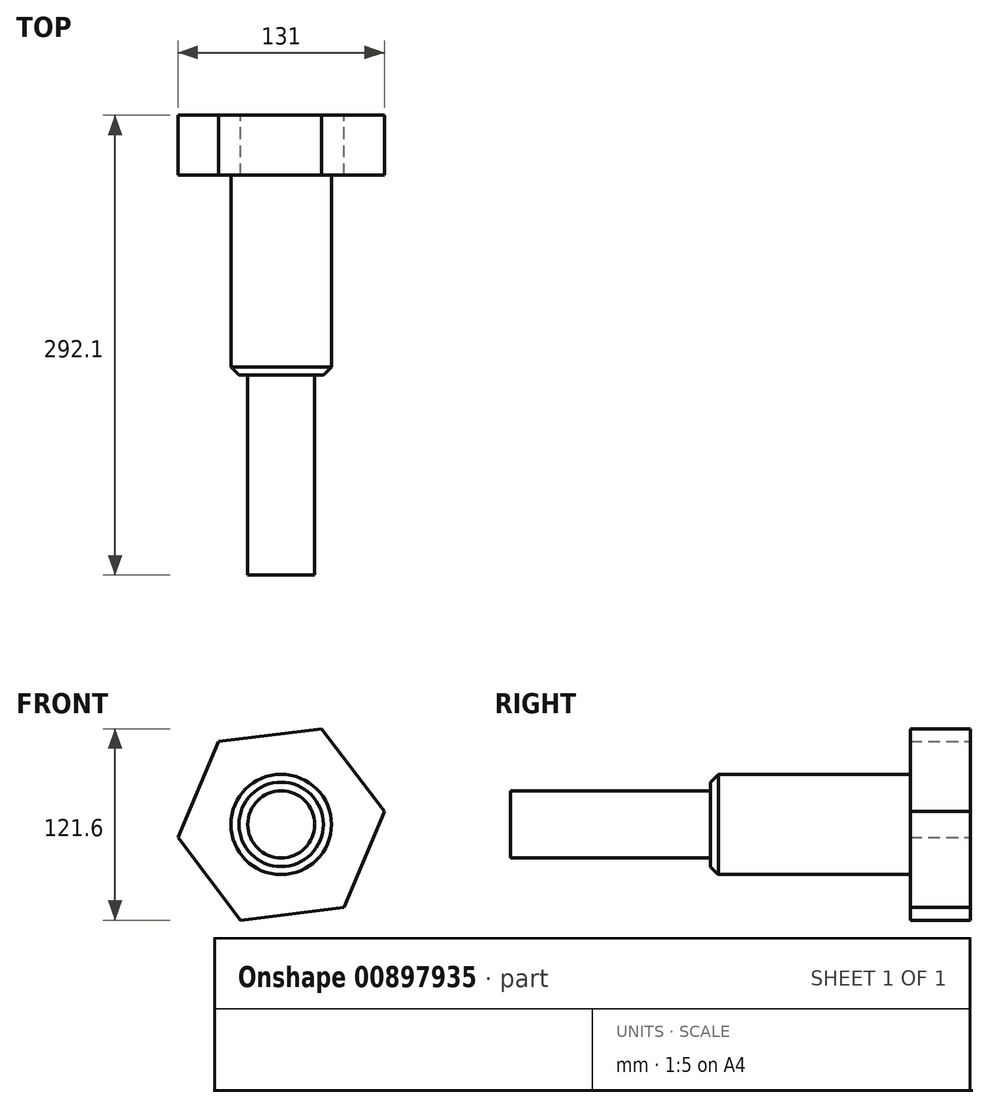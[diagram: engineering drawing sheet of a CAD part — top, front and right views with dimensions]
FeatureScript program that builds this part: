
annotation { "Feature Type Name" : "Feature", "Feature Type Description" : "" }
export const myFeature = defineFeature(function(context is Context, id is Id, definition is map)
    precondition{}
    {
        {
            var Q0;
            Q0=qCreatedBy(makeId("Front.planeOp"),FACE);
            var sketch = newSketch(context, id + "F0", { "sketchPlane" : qUnion([Q0])});
            skCircle(sketch, "E0.cCircle", {"center": v(0, 0) * mm, "radius": 57.16 * mm, "construction": true});
            skLineSegment(sketch, "E0.0", {"start": v(65.5, 8.14) * mm, "end": v(39.8, -52.66) * mm});
            skLineSegment(sketch, "E0.1", {"start": v(39.8, -52.66) * mm, "end": v(-25.7, -60.8) * mm});
            skLineSegment(sketch, "E0.2", {"start": v(-25.7, -60.8) * mm, "end": v(-65.5, -8.14) * mm});
            skLineSegment(sketch, "E0.3", {"start": v(-65.5, -8.14) * mm, "end": v(-39.8, 52.66) * mm});
            skLineSegment(sketch, "E0.4", {"start": v(-39.8, 52.66) * mm, "end": v(25.7, 60.8) * mm});
            skLineSegment(sketch, "E0.5", {"start": v(25.7, 60.8) * mm, "end": v(65.5, 8.14) * mm});
            skPoint(sketch, "E0.0.midPoint", {"position": v(52.65, -22.26) * mm});
            skSolve(sketch);
        }
        {
            var Q0;
            Q0=makeQuery(id+"F0.imprint","IMPRINT",FACE,{"disambiguationData":[TD([[makeQuery(id+"F0.imprint","IMPRINT",EDGE,{"derivedFrom":sQuery(id+"F0.wireOp",EDGE,"E0.0")}),-1.0]])]});
            extrude(context, id + "F1", {"entities" : qUnion([Q0]), "depth" : 38.1 * mm, "offsetDistance" : 25.4 * mm});
        }
        {
            var Q0;
            Q0=makeQuery(id+"F1.opExtrude","CAP_FACE",FACE,{"disambiguationData":[OSD([sQuery(id+"F0.wireOp",EDGE,"E0.0"),sQuery(id+"F0.wireOp",EDGE,"E0.1"),sQuery(id+"F0.wireOp",EDGE,"E0.2"),sQuery(id+"F0.wireOp",EDGE,"E0.3"),sQuery(id+"F0.wireOp",EDGE,"E0.4"),sQuery(id+"F0.wireOp",EDGE,"E0.5")])],"isStart":false});
            var sketch = newSketch(context, id + "F2", { "sketchPlane" : qUnion([Q0])});
            skCircle(sketch, "E1", {"center": v(0, 0) * mm, "radius": 31.88 * mm});
            skSolve(sketch);
        }
        {
            var Q0;
            Q0=makeQuery(id+"F2.imprint","IMPRINT",FACE,{"disambiguationData":[TD([[makeQuery(id+"F2.imprint","IMPRINT",EDGE,{"derivedFrom":sQuery(id+"F2.wireOp",EDGE,"E1")}),1.0]])]});
            extrude(context, id + "F3", {"entities" : qUnion([Q0]), "operationType" : NewBodyOperationType.ADD, "depth" : 127 * mm, "offsetDistance" : 25.4 * mm});
        }
        {
            var Q0;
            Q0=makeQuery(id+"F3.opExtrude","CAP_FACE",FACE,{"disambiguationData":[OSD([sQuery(id+"F2.wireOp",EDGE,"E1")])],"isStart":false});
            chamfer(context, id + "F4", {"entities" : qUnion([Q0]), "width" : 5.08 * mm, "tangentPropagation" : true});
        }
        {
            var Q0;
            Q0=makeQuery(id+"F3.opExtrude","CAP_FACE",FACE,{"disambiguationData":[OSD([sQuery(id+"F2.wireOp",EDGE,"E1")])],"isStart":false});
            var sketch = newSketch(context, id + "F5", { "sketchPlane" : qUnion([Q0])});
            skCircle(sketch, "E2", {"center": v(0, 0) * mm, "radius": 21.26 * mm});
            skSolve(sketch);
        }
        {
            var Q0;
            Q0 = qSketchRegion(id + "F5", true);
            extrude(context, id + "F6", {"entities" : qUnion([Q0]), "operationType" : NewBodyOperationType.ADD, "depth" : 127 * mm, "offsetDistance" : 25.4 * mm});
        }
    });
